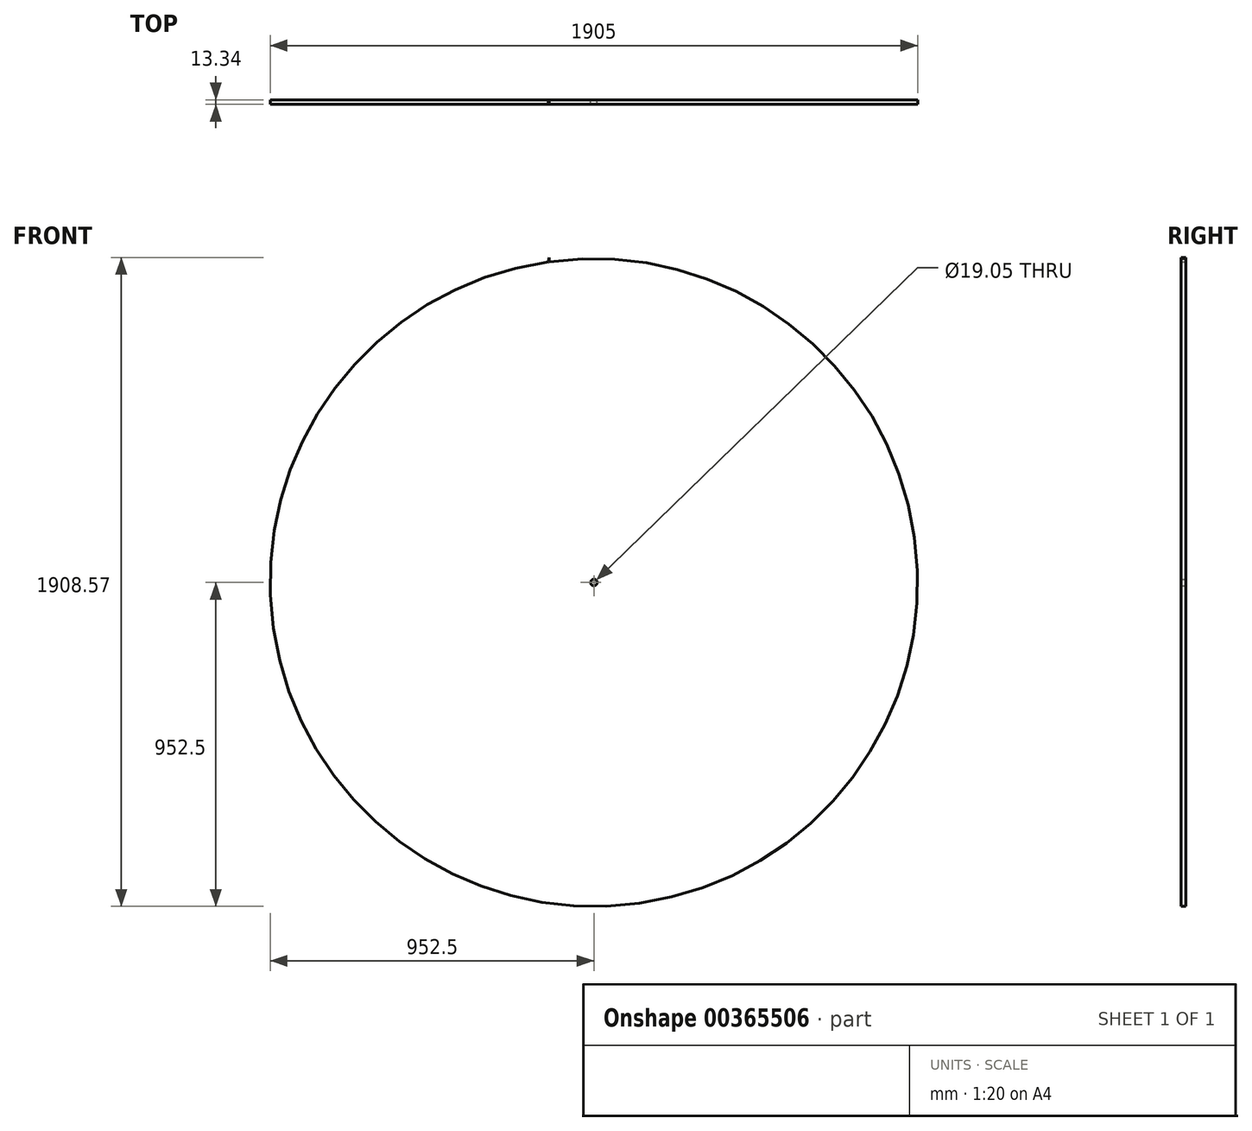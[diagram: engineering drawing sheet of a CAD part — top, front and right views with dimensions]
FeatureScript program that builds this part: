
annotation { "Feature Type Name" : "Feature", "Feature Type Description" : "" }
export const myFeature = defineFeature(function(context is Context, id is Id, definition is map)
    precondition{}
    {
        {
            var Q0;
            Q0=qCreatedBy(makeId("Front.planeOp"),FACE);
            var sketch = newSketch(context, id + "F0", { "sketchPlane" : qUnion([Q0])});
            skCircle(sketch, "E0", {"center": v(0, 0) * mm, "radius": 952.5 * mm});
            skCircle(sketch, "E1", {"center": v(0, 0) * mm, "radius": 3.3 * mm});
            skLineSegment(sketch, "E2", {"start": v(-131.54, 943.37) * mm, "end": v(-131.54, 956.07) * mm});
            skLineSegment(sketch, "E3", {"start": v(-131.54, 956.07) * mm, "end": v(-134.68, 942.93) * mm});
            skCircle(sketch, "E4.MirrorC", {"center": v(0, 0) * mm, "radius": 9.53 * mm});
            skLineSegment(sketch, "E5", {"start": v(0, 9.53) * mm, "end": v(0, 15.92) * mm});
            skSolve(sketch);
        }
        {
            var Q0;
            Q0 = qSketchRegion(id + "F0", true);
            extrude(context, id + "F1", {"entities" : qUnion([Q0]), "depth" : 13.33 * mm});
        }
    });
